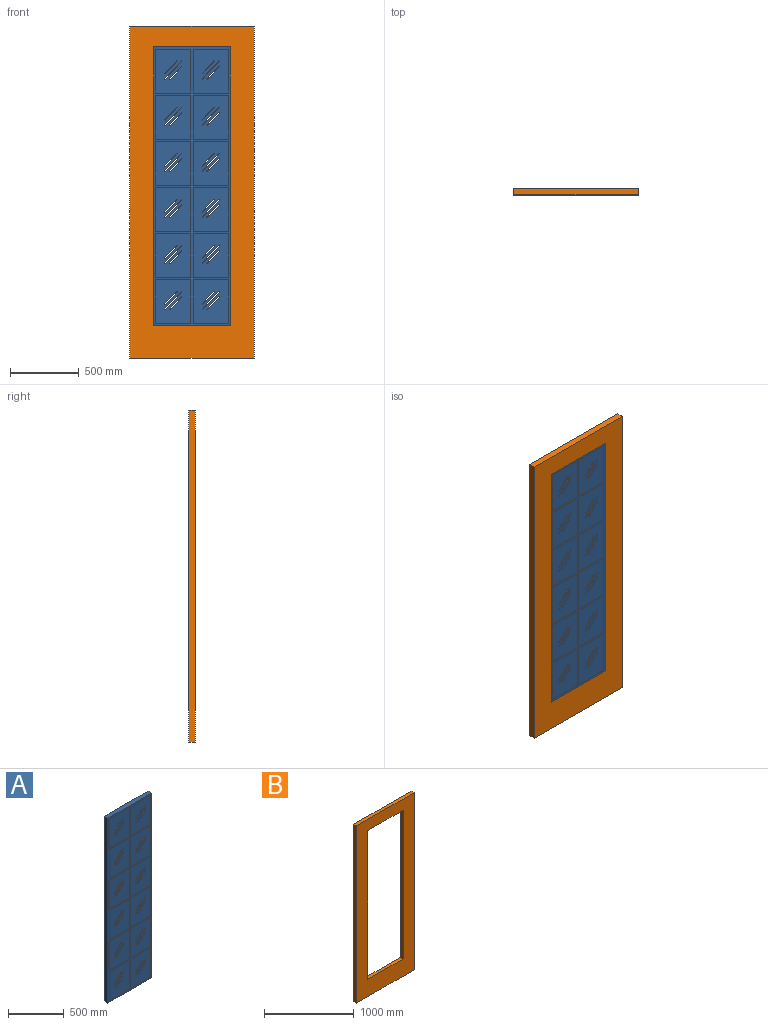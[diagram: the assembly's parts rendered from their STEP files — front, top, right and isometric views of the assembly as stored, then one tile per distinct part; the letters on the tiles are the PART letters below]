
ASSEMBLY  parts=2 mates=1
PART A: 270 faces, bbox 558.8x44.5x2032 mm
  f0: plane 320.15x0.64mm, normal (1,0,0), area 203.3mm2, adj f1,f3,f101,f269
  f1: plane 255.59x0.64mm, normal (0,0,-1), area 162.3mm2, adj f0,f2,f101,f269
  f2: plane 320.15x0.64mm, normal (-1,0,0), area 203.3mm2, adj f1,f3,f101,f269
  f3: plane 255.59x0.64mm, normal (0,0,1), area 162.3mm2, adj f0,f2,f101,f269
  f4: plane 255.59x0.64mm, normal (0,0,-1), area 162.3mm2, adj f5,f7,f101,f255
  f5: plane 320.15x0.64mm, normal (-1,0,0), area 203.3mm2, adj f4,f6,f101,f255
  f6: plane 255.59x0.64mm, normal (0,0,1), area 162.3mm2, adj f5,f7,f101,f255
  f7: plane 320.15x0.64mm, normal (1,0,0), area 203.3mm2, adj f4,f6,f101,f255
  f8: plane 320.15x0.64mm, normal (1,0,0), area 203.3mm2, adj f9,f11,f101,f241
  f9: plane 255.59x0.64mm, normal (0,0,-1), area 162.3mm2, adj f8,f10,f101,f241
  f10: plane 320.15x0.64mm, normal (-1,0,0), area 203.3mm2, adj f9,f11,f101,f241
  f11: plane 255.59x0.64mm, normal (0,0,1), area 162.3mm2, adj f8,f10,f101,f241
  f12: plane 320.15x0.64mm, normal (1,0,0), area 203.3mm2, adj f13,f15,f101,f227
  f13: plane 255.59x0.64mm, normal (0,0,-1), area 162.3mm2, adj f12,f14,f101,f227
  f14: plane 320.15x0.64mm, normal (-1,0,0), area 203.3mm2, adj f13,f15,f101,f227
  f15: plane 255.59x0.64mm, normal (0,0,1), area 162.3mm2, adj f12,f14,f101,f227
  f16: plane 255.59x0.64mm, normal (0,0,-1), area 162.3mm2, adj f17,f19,f101,f213
  f17: plane 320.15x0.64mm, normal (-1,0,0), area 203.3mm2, adj f16,f18,f101,f213
  f18: plane 255.59x0.64mm, normal (0,0,1), area 162.3mm2, adj f17,f19,f101,f213
  f19: plane 320.15x0.64mm, normal (1,0,0), area 203.3mm2, adj f16,f18,f101,f213
  f20: plane 320.15x0.64mm, normal (1,0,0), area 203.3mm2, adj f21,f23,f101,f199
  f21: plane 255.59x0.64mm, normal (0,0,-1), area 162.3mm2, adj f20,f22,f101,f199
  f22: plane 320.15x0.64mm, normal (-1,0,0), area 203.3mm2, adj f21,f23,f101,f199
  f23: plane 255.59x0.64mm, normal (0,0,1), area 162.3mm2, adj f20,f22,f101,f199
  f24: plane 320.15x0.64mm, normal (1,0,0), area 203.3mm2, adj f25,f27,f101,f185
  f25: plane 255.59x0.64mm, normal (0,0,-1), area 162.3mm2, adj f24,f26,f101,f185
  f26: plane 320.15x0.64mm, normal (-1,0,0), area 203.3mm2, adj f25,f27,f101,f185
  f27: plane 255.59x0.64mm, normal (0,0,1), area 162.3mm2, adj f24,f26,f101,f185
  f28: plane 255.59x0.64mm, normal (0,0,-1), area 162.3mm2, adj f29,f31,f101,f171
  f29: plane 320.15x0.64mm, normal (-1,0,0), area 203.3mm2, adj f28,f30,f101,f171
  f30: plane 255.59x0.64mm, normal (0,0,1), area 162.3mm2, adj f29,f31,f101,f171
  f31: plane 320.15x0.64mm, normal (1,0,0), area 203.3mm2, adj f28,f30,f101,f171
  f32: plane 255.59x0.64mm, normal (0,0,-1), area 162.3mm2, adj f33,f35,f101,f157
  f33: plane 320.15x0.64mm, normal (-1,0,0), area 203.3mm2, adj f32,f34,f101,f157
  f34: plane 255.59x0.64mm, normal (0,0,1), area 162.3mm2, adj f33,f35,f101,f157
  f35: plane 320.15x0.64mm, normal (1,0,0), area 203.3mm2, adj f32,f34,f101,f157
  f36: plane 320.15x0.64mm, normal (1,0,0), area 203.3mm2, adj f37,f39,f101,f143
  f37: plane 255.59x0.64mm, normal (0,0,-1), area 162.3mm2, adj f36,f38,f101,f143
  f38: plane 320.15x0.64mm, normal (-1,0,0), area 203.3mm2, adj f37,f39,f101,f143
  f39: plane 255.59x0.64mm, normal (0,0,1), area 162.3mm2, adj f36,f38,f101,f143
  f40: plane 320.15x0.64mm, normal (1,0,0), area 203.3mm2, adj f41,f43,f101,f129
  f41: plane 255.59x0.64mm, normal (0,0,-1), area 162.3mm2, adj f40,f42,f101,f129
  f42: plane 320.15x0.64mm, normal (-1,0,0), area 203.3mm2, adj f41,f43,f101,f129
  f43: plane 255.59x0.64mm, normal (0,0,1), area 162.3mm2, adj f40,f42,f101,f129
  f44: plane 255.59x0.64mm, normal (0,0,-1), area 162.3mm2, adj f45,f47,f101,f115
  f45: plane 320.15x0.64mm, normal (-1,0,0), area 203.3mm2, adj f44,f46,f101,f115
  f46: plane 255.59x0.64mm, normal (0,0,1), area 162.3mm2, adj f45,f47,f101,f115
  f47: plane 320.15x0.64mm, normal (1,0,0), area 203.3mm2, adj f44,f46,f101,f115
  f48: plane 320.15x0.64mm, normal (1,0,0), area 203.3mm2, adj f49,f99,f100,f268
  f49: plane 255.59x0.64mm, normal (0,0,-1), area 162.3mm2, adj f48,f50,f100,f268
  f50: plane 320.15x0.64mm, normal (-1,0,0), area 203.3mm2, adj f49,f99,f100,f268
  f51: plane 320.15x0.64mm, normal (1,0,0), area 203.3mm2, adj f52,f87,f100,f128
  f52: plane 255.59x0.64mm, normal (0,0,-1), area 162.3mm2, adj f51,f53,f100,f128
  f53: plane 320.15x0.64mm, normal (-1,0,0), area 203.3mm2, adj f52,f87,f100,f128
  f54: plane 320.15x0.64mm, normal (1,0,0), area 203.3mm2, adj f55,f88,f100,f142
  f55: plane 255.59x0.64mm, normal (0,0,-1), area 162.3mm2, adj f54,f56,f100,f142
  f56: plane 320.15x0.64mm, normal (-1,0,0), area 203.3mm2, adj f55,f88,f100,f142
  f57: plane 320.15x0.64mm, normal (1,0,0), area 203.3mm2, adj f58,f89,f100,f184
  f58: plane 255.59x0.64mm, normal (0,0,-1), area 162.3mm2, adj f57,f59,f100,f184
  f59: plane 320.15x0.64mm, normal (-1,0,0), area 203.3mm2, adj f58,f89,f100,f184
  f60: plane 320.15x0.64mm, normal (1,0,0), area 203.3mm2, adj f61,f90,f100,f198
  f61: plane 255.59x0.64mm, normal (0,0,-1), area 162.3mm2, adj f60,f62,f100,f198
  f62: plane 320.15x0.64mm, normal (-1,0,0), area 203.3mm2, adj f61,f90,f100,f198
  f63: plane 320.15x0.64mm, normal (1,0,0), area 203.3mm2, adj f64,f91,f100,f240
  f64: plane 255.59x0.64mm, normal (0,0,-1), area 162.3mm2, adj f63,f65,f100,f240
  f65: plane 320.15x0.64mm, normal (-1,0,0), area 203.3mm2, adj f64,f91,f100,f240
  f66: plane 320.15x0.64mm, normal (1,0,0), area 203.3mm2, adj f67,f92,f100,f226
  f67: plane 255.59x0.64mm, normal (0,0,-1), area 162.3mm2, adj f66,f68,f100,f226
  f68: plane 320.15x0.64mm, normal (-1,0,0), area 203.3mm2, adj f67,f92,f100,f226
  f69: plane 558.8x44.45mm, normal (0,0,1), area 24838.7mm2, adj f70,f93,f100,f101
  f70: plane 2032x44.45mm, normal (-1,0,0), area 90322.4mm2, adj f69,f71,f100,f101
  f71: plane 558.8x44.45mm, normal (0,0,-1), area 24838.7mm2, adj f70,f93,f100,f101
  f72: plane 255.59x0.64mm, normal (0,0,-1), area 162.3mm2, adj f73,f94,f100,f212
  f73: plane 320.15x0.64mm, normal (-1,0,0), area 203.3mm2, adj f72,f74,f100,f212
  f74: plane 255.59x0.64mm, normal (0,0,1), area 162.3mm2, adj f73,f94,f100,f212
  f75: plane 255.59x0.64mm, normal (0,0,-1), area 162.3mm2, adj f76,f95,f100,f170
  f76: plane 320.15x0.64mm, normal (-1,0,0), area 203.3mm2, adj f75,f77,f100,f170
  f77: plane 255.59x0.64mm, normal (0,0,1), area 162.3mm2, adj f76,f95,f100,f170
  f78: plane 255.59x0.64mm, normal (0,0,-1), area 162.3mm2, adj f79,f96,f100,f156
  f79: plane 320.15x0.64mm, normal (-1,0,0), area 203.3mm2, adj f78,f80,f100,f156
  f80: plane 255.59x0.64mm, normal (0,0,1), area 162.3mm2, adj f79,f96,f100,f156
  f81: plane 255.59x0.64mm, normal (0,0,-1), area 162.3mm2, adj f82,f97,f100,f114
  f82: plane 320.15x0.64mm, normal (-1,0,0), area 203.3mm2, adj f81,f83,f100,f114
  f83: plane 255.59x0.64mm, normal (0,0,1), area 162.3mm2, adj f82,f97,f100,f114
  f84: plane 255.59x0.64mm, normal (0,0,-1), area 162.3mm2, adj f85,f98,f100,f254
  f85: plane 320.15x0.64mm, normal (-1,0,0), area 203.3mm2, adj f84,f86,f100,f254
  f86: plane 255.59x0.64mm, normal (0,0,1), area 162.3mm2, adj f85,f98,f100,f254
  f87: plane 255.59x0.64mm, normal (0,0,1), area 162.3mm2, adj f51,f53,f100,f128
  f88: plane 255.59x0.64mm, normal (0,0,1), area 162.3mm2, adj f54,f56,f100,f142
  f89: plane 255.59x0.64mm, normal (0,0,1), area 162.3mm2, adj f57,f59,f100,f184
  f90: plane 255.59x0.64mm, normal (0,0,1), area 162.3mm2, adj f60,f62,f100,f198
  f91: plane 255.59x0.64mm, normal (0,0,1), area 162.3mm2, adj f63,f65,f100,f240
  f92: plane 255.59x0.64mm, normal (0,0,1), area 162.3mm2, adj f66,f68,f100,f226
  f93: plane 2032x44.45mm, normal (1,0,0), area 90322.4mm2, adj f69,f71,f100,f101
  f94: plane 320.15x0.64mm, normal (1,0,0), area 203.3mm2, adj f72,f74,f100,f212
  f95: plane 320.15x0.64mm, normal (1,0,0), area 203.3mm2, adj f75,f77,f100,f170
  f96: plane 320.15x0.64mm, normal (1,0,0), area 203.3mm2, adj f78,f80,f100,f156
  f97: plane 320.15x0.64mm, normal (1,0,0), area 203.3mm2, adj f81,f83,f100,f114
  f98: plane 320.15x0.64mm, normal (1,0,0), area 203.3mm2, adj f84,f86,f100,f254
  f99: plane 255.59x0.64mm, normal (0,0,1), area 162.3mm2, adj f48,f50,f100,f268
  f100: plane 2032x558.8mm, normal (0,-1,0), area 153578.3mm2, adj f48,f49,f50,f51,f52,f53,f54,f55
  f101: plane 2032x558.8mm, normal (0,1,0), area 153578.3mm2, adj f0,f1,f2,f3,f4,f5,f6,f7
  f102: cylinder r=3.17mm len=43.18mm, axis (0,1,0), area 430.7mm2, adj f103,f113,f114,f115
  f103: plane 88.11x82.76mm, normal (-0.73,0,0.68), area 5219.7mm2, adj f102,f104,f114,f115
  f104: cylinder r=3.17mm len=43.18mm, axis (0,1,0), area 430.7mm2, adj f103,f113,f114,f115
  f105: cylinder r=3.17mm len=43.18mm, axis (0,1,0), area 430.7mm2, adj f106,f111,f114,f115
  f106: plane 88.11x82.76mm, normal (-0.73,0,0.68), area 5219.7mm2, adj f105,f107,f114,f115
  f107: cylinder r=3.17mm len=43.18mm, axis (0,1,0), area 430.7mm2, adj f106,f111,f114,f115
  f108: plane 126.21x118.54mm, normal (0.73,0,-0.68), area 7476.7mm2, adj f109,f112,f114,f115
  f109: cylinder r=3.17mm len=43.18mm, axis (0,1,0), area 430.7mm2, adj f108,f110,f114,f115
  f110: plane 126.21x118.54mm, normal (-0.73,0,0.68), area 7476.7mm2, adj f109,f112,f114,f115
  f111: plane 88.11x82.76mm, normal (0.73,0,-0.68), area 5219.7mm2, adj f105,f107,f114,f115
  f112: cylinder r=3.17mm len=43.18mm, axis (0,1,0), area 430.7mm2, adj f108,f110,f114,f115
  f113: plane 88.11x82.76mm, normal (0.73,0,-0.68), area 5219.7mm2, adj f102,f104,f114,f115
  f114: plane 320.15x255.59mm, normal (0,-1,0), area 79095.5mm2, adj f81,f82,f83,f97,f102,f103,f104,f105
  f115: plane 320.15x255.59mm, normal (0,1,0), area 79095.5mm2, adj f44,f45,f46,f47,f102,f103,f104,f105
  f116: cylinder r=3.17mm len=43.18mm, axis (0,1,0), area 430.7mm2, adj f117,f127,f128,f129
  f117: plane 88.11x82.76mm, normal (-0.73,0,0.68), area 5219.7mm2, adj f116,f118,f128,f129
  f118: cylinder r=3.17mm len=43.18mm, axis (0,1,0), area 430.7mm2, adj f117,f127,f128,f129
  f119: cylinder r=3.17mm len=43.18mm, axis (0,1,0), area 430.7mm2, adj f120,f125,f128,f129
  f120: plane 88.11x82.76mm, normal (-0.73,0,0.68), area 5219.7mm2, adj f119,f121,f128,f129
  f121: cylinder r=3.17mm len=43.18mm, axis (0,1,0), area 430.7mm2, adj f120,f125,f128,f129
  f122: plane 126.21x118.54mm, normal (0.73,0,-0.68), area 7476.7mm2, adj f123,f126,f128,f129
  f123: cylinder r=3.17mm len=43.18mm, axis (0,1,0), area 430.7mm2, adj f122,f124,f128,f129
  f124: plane 126.21x118.54mm, normal (-0.73,0,0.68), area 7476.7mm2, adj f123,f126,f128,f129
  f125: plane 88.11x82.76mm, normal (0.73,0,-0.68), area 5219.7mm2, adj f119,f121,f128,f129
  f126: cylinder r=3.17mm len=43.18mm, axis (0,1,0), area 430.7mm2, adj f122,f124,f128,f129
  f127: plane 88.11x82.76mm, normal (0.73,0,-0.68), area 5219.7mm2, adj f116,f118,f128,f129
  f128: plane 320.15x255.59mm, normal (0,-1,0), area 79095.5mm2, adj f51,f52,f53,f87,f116,f117,f118,f119
  f129: plane 320.15x255.59mm, normal (0,1,0), area 79095.5mm2, adj f40,f41,f42,f43,f116,f117,f118,f119
  f130: cylinder r=3.17mm len=43.18mm, axis (0,1,0), area 430.7mm2, adj f131,f141,f142,f143
  f131: plane 88.11x82.76mm, normal (-0.73,0,0.68), area 5219.7mm2, adj f130,f132,f142,f143
  f132: cylinder r=3.17mm len=43.18mm, axis (0,1,0), area 430.7mm2, adj f131,f141,f142,f143
  f133: cylinder r=3.17mm len=43.18mm, axis (0,1,0), area 430.7mm2, adj f134,f139,f142,f143
  f134: plane 88.11x82.76mm, normal (-0.73,0,0.68), area 5219.7mm2, adj f133,f135,f142,f143
  f135: cylinder r=3.17mm len=43.18mm, axis (0,1,0), area 430.7mm2, adj f134,f139,f142,f143
  f136: plane 126.21x118.54mm, normal (0.73,0,-0.68), area 7476.7mm2, adj f137,f140,f142,f143
  f137: cylinder r=3.17mm len=43.18mm, axis (0,1,0), area 430.7mm2, adj f136,f138,f142,f143
  f138: plane 126.21x118.54mm, normal (-0.73,0,0.68), area 7476.7mm2, adj f137,f140,f142,f143
  f139: plane 88.11x82.76mm, normal (0.73,0,-0.68), area 5219.7mm2, adj f133,f135,f142,f143
  f140: cylinder r=3.17mm len=43.18mm, axis (0,1,0), area 430.7mm2, adj f136,f138,f142,f143
  f141: plane 88.11x82.76mm, normal (0.73,0,-0.68), area 5219.7mm2, adj f130,f132,f142,f143
  f142: plane 320.15x255.59mm, normal (0,-1,0), area 79095.5mm2, adj f54,f55,f56,f88,f130,f131,f132,f133
  f143: plane 320.15x255.59mm, normal (0,1,0), area 79095.5mm2, adj f36,f37,f38,f39,f130,f131,f132,f133
  f144: cylinder r=3.17mm len=43.18mm, axis (0,1,0), area 430.7mm2, adj f145,f155,f156,f157
  f145: plane 88.11x82.76mm, normal (-0.73,0,0.68), area 5219.7mm2, adj f144,f146,f156,f157
  f146: cylinder r=3.17mm len=43.18mm, axis (0,1,0), area 430.7mm2, adj f145,f155,f156,f157
  f147: cylinder r=3.17mm len=43.18mm, axis (0,1,0), area 430.7mm2, adj f148,f153,f156,f157
  f148: plane 88.11x82.76mm, normal (-0.73,0,0.68), area 5219.7mm2, adj f147,f149,f156,f157
  f149: cylinder r=3.17mm len=43.18mm, axis (0,1,0), area 430.7mm2, adj f148,f153,f156,f157
  f150: plane 126.21x118.54mm, normal (0.73,0,-0.68), area 7476.7mm2, adj f151,f154,f156,f157
  f151: cylinder r=3.17mm len=43.18mm, axis (0,1,0), area 430.7mm2, adj f150,f152,f156,f157
  f152: plane 126.21x118.54mm, normal (-0.73,0,0.68), area 7476.7mm2, adj f151,f154,f156,f157
  f153: plane 88.11x82.76mm, normal (0.73,0,-0.68), area 5219.7mm2, adj f147,f149,f156,f157
  f154: cylinder r=3.17mm len=43.18mm, axis (0,1,0), area 430.7mm2, adj f150,f152,f156,f157
  f155: plane 88.11x82.76mm, normal (0.73,0,-0.68), area 5219.7mm2, adj f144,f146,f156,f157
  f156: plane 320.15x255.59mm, normal (0,-1,0), area 79095.5mm2, adj f78,f79,f80,f96,f144,f145,f146,f147
  f157: plane 320.15x255.59mm, normal (0,1,0), area 79095.5mm2, adj f32,f33,f34,f35,f144,f145,f146,f147
  f158: cylinder r=3.17mm len=43.18mm, axis (0,1,0), area 430.7mm2, adj f159,f169,f170,f171
  f159: plane 88.11x82.76mm, normal (-0.73,0,0.68), area 5219.7mm2, adj f158,f160,f170,f171
  f160: cylinder r=3.17mm len=43.18mm, axis (0,1,0), area 430.7mm2, adj f159,f169,f170,f171
  f161: cylinder r=3.17mm len=43.18mm, axis (0,1,0), area 430.7mm2, adj f162,f167,f170,f171
  f162: plane 88.11x82.76mm, normal (-0.73,0,0.68), area 5219.7mm2, adj f161,f163,f170,f171
  f163: cylinder r=3.17mm len=43.18mm, axis (0,1,0), area 430.7mm2, adj f162,f167,f170,f171
  f164: plane 126.21x118.54mm, normal (0.73,0,-0.68), area 7476.7mm2, adj f165,f168,f170,f171
  f165: cylinder r=3.17mm len=43.18mm, axis (0,1,0), area 430.7mm2, adj f164,f166,f170,f171
  f166: plane 126.21x118.54mm, normal (-0.73,0,0.68), area 7476.7mm2, adj f165,f168,f170,f171
  f167: plane 88.11x82.76mm, normal (0.73,0,-0.68), area 5219.7mm2, adj f161,f163,f170,f171
  f168: cylinder r=3.17mm len=43.18mm, axis (0,1,0), area 430.7mm2, adj f164,f166,f170,f171
  f169: plane 88.11x82.76mm, normal (0.73,0,-0.68), area 5219.7mm2, adj f158,f160,f170,f171
  f170: plane 320.15x255.59mm, normal (0,-1,0), area 79095.5mm2, adj f75,f76,f77,f95,f158,f159,f160,f161
  f171: plane 320.15x255.59mm, normal (0,1,0), area 79095.5mm2, adj f28,f29,f30,f31,f158,f159,f160,f161
  f172: cylinder r=3.17mm len=43.18mm, axis (0,1,0), area 430.7mm2, adj f173,f183,f184,f185
  f173: plane 88.11x82.76mm, normal (-0.73,0,0.68), area 5219.7mm2, adj f172,f174,f184,f185
  f174: cylinder r=3.17mm len=43.18mm, axis (0,1,0), area 430.7mm2, adj f173,f183,f184,f185
  f175: cylinder r=3.17mm len=43.18mm, axis (0,1,0), area 430.7mm2, adj f176,f181,f184,f185
  f176: plane 88.11x82.76mm, normal (-0.73,0,0.68), area 5219.7mm2, adj f175,f177,f184,f185
  f177: cylinder r=3.17mm len=43.18mm, axis (0,1,0), area 430.7mm2, adj f176,f181,f184,f185
  f178: plane 126.21x118.54mm, normal (0.73,0,-0.68), area 7476.7mm2, adj f179,f182,f184,f185
  f179: cylinder r=3.17mm len=43.18mm, axis (0,1,0), area 430.7mm2, adj f178,f180,f184,f185
  f180: plane 126.21x118.54mm, normal (-0.73,0,0.68), area 7476.7mm2, adj f179,f182,f184,f185
  f181: plane 88.11x82.76mm, normal (0.73,0,-0.68), area 5219.7mm2, adj f175,f177,f184,f185
  f182: cylinder r=3.17mm len=43.18mm, axis (0,1,0), area 430.7mm2, adj f178,f180,f184,f185
  f183: plane 88.11x82.76mm, normal (0.73,0,-0.68), area 5219.7mm2, adj f172,f174,f184,f185
  f184: plane 320.15x255.59mm, normal (0,-1,0), area 79095.5mm2, adj f57,f58,f59,f89,f172,f173,f174,f175
  f185: plane 320.15x255.59mm, normal (0,1,0), area 79095.5mm2, adj f24,f25,f26,f27,f172,f173,f174,f175
  f186: cylinder r=3.17mm len=43.18mm, axis (0,1,0), area 430.7mm2, adj f187,f197,f198,f199
  f187: plane 88.11x82.76mm, normal (-0.73,0,0.68), area 5219.7mm2, adj f186,f188,f198,f199
  f188: cylinder r=3.17mm len=43.18mm, axis (0,1,0), area 430.7mm2, adj f187,f197,f198,f199
  f189: cylinder r=3.17mm len=43.18mm, axis (0,1,0), area 430.7mm2, adj f190,f195,f198,f199
  f190: plane 88.11x82.76mm, normal (-0.73,0,0.68), area 5219.7mm2, adj f189,f191,f198,f199
  f191: cylinder r=3.17mm len=43.18mm, axis (0,1,0), area 430.7mm2, adj f190,f195,f198,f199
  f192: plane 126.21x118.54mm, normal (0.73,0,-0.68), area 7476.7mm2, adj f193,f196,f198,f199
  f193: cylinder r=3.17mm len=43.18mm, axis (0,1,0), area 430.7mm2, adj f192,f194,f198,f199
  f194: plane 126.21x118.54mm, normal (-0.73,0,0.68), area 7476.7mm2, adj f193,f196,f198,f199
  f195: plane 88.11x82.76mm, normal (0.73,0,-0.68), area 5219.7mm2, adj f189,f191,f198,f199
  f196: cylinder r=3.17mm len=43.18mm, axis (0,1,0), area 430.7mm2, adj f192,f194,f198,f199
  f197: plane 88.11x82.76mm, normal (0.73,0,-0.68), area 5219.7mm2, adj f186,f188,f198,f199
  f198: plane 320.15x255.59mm, normal (0,-1,0), area 79095.5mm2, adj f60,f61,f62,f90,f186,f187,f188,f189
  f199: plane 320.15x255.59mm, normal (0,1,0), area 79095.5mm2, adj f20,f21,f22,f23,f186,f187,f188,f189
  f200: cylinder r=3.17mm len=43.18mm, axis (0,1,0), area 430.7mm2, adj f201,f211,f212,f213
  f201: plane 88.11x82.76mm, normal (-0.73,0,0.68), area 5219.7mm2, adj f200,f202,f212,f213
  f202: cylinder r=3.17mm len=43.18mm, axis (0,1,0), area 430.7mm2, adj f201,f211,f212,f213
  f203: cylinder r=3.17mm len=43.18mm, axis (0,1,0), area 430.7mm2, adj f204,f209,f212,f213
  f204: plane 88.11x82.76mm, normal (-0.73,0,0.68), area 5219.7mm2, adj f203,f205,f212,f213
  f205: cylinder r=3.17mm len=43.18mm, axis (0,1,0), area 430.7mm2, adj f204,f209,f212,f213
  f206: plane 126.21x118.54mm, normal (0.73,0,-0.68), area 7476.7mm2, adj f207,f210,f212,f213
  f207: cylinder r=3.17mm len=43.18mm, axis (0,1,0), area 430.7mm2, adj f206,f208,f212,f213
  f208: plane 126.21x118.54mm, normal (-0.73,0,0.68), area 7476.7mm2, adj f207,f210,f212,f213
  f209: plane 88.11x82.76mm, normal (0.73,0,-0.68), area 5219.7mm2, adj f203,f205,f212,f213
  f210: cylinder r=3.17mm len=43.18mm, axis (0,1,0), area 430.7mm2, adj f206,f208,f212,f213
  f211: plane 88.11x82.76mm, normal (0.73,0,-0.68), area 5219.7mm2, adj f200,f202,f212,f213
  f212: plane 320.15x255.59mm, normal (0,-1,0), area 79095.5mm2, adj f72,f73,f74,f94,f200,f201,f202,f203
  f213: plane 320.15x255.59mm, normal (0,1,0), area 79095.5mm2, adj f16,f17,f18,f19,f200,f201,f202,f203
  f214: plane 88.11x82.76mm, normal (-0.73,0,0.68), area 5219.7mm2, adj f215,f225,f226,f227
  f215: cylinder r=3.17mm len=43.18mm, axis (0,1,0), area 430.7mm2, adj f214,f216,f226,f227
  f216: plane 88.11x82.76mm, normal (0.73,0,-0.68), area 5219.7mm2, adj f215,f225,f226,f227
  f217: plane 88.11x82.76mm, normal (-0.73,0,0.68), area 5219.7mm2, adj f218,f223,f226,f227
  f218: cylinder r=3.17mm len=43.18mm, axis (0,1,0), area 430.7mm2, adj f217,f219,f226,f227
  f219: plane 88.11x82.76mm, normal (0.73,0,-0.68), area 5219.7mm2, adj f218,f223,f226,f227
  f220: plane 126.21x118.54mm, normal (-0.73,0,0.68), area 7476.7mm2, adj f221,f224,f226,f227
  f221: cylinder r=3.17mm len=43.18mm, axis (0,1,0), area 430.7mm2, adj f220,f222,f226,f227
  f222: plane 126.21x118.54mm, normal (0.73,0,-0.68), area 7476.7mm2, adj f221,f224,f226,f227
  f223: cylinder r=3.17mm len=43.18mm, axis (0,1,0), area 430.7mm2, adj f217,f219,f226,f227
  f224: cylinder r=3.17mm len=43.18mm, axis (0,1,0), area 430.7mm2, adj f220,f222,f226,f227
  f225: cylinder r=3.17mm len=43.18mm, axis (0,1,0), area 430.7mm2, adj f214,f216,f226,f227
  f226: plane 320.15x255.59mm, normal (0,-1,0), area 79095.5mm2, adj f66,f67,f68,f92,f214,f215,f216,f217
  f227: plane 320.15x255.59mm, normal (0,1,0), area 79095.5mm2, adj f12,f13,f14,f15,f214,f215,f216,f217
  f228: cylinder r=3.17mm len=43.18mm, axis (0,1,0), area 430.7mm2, adj f229,f239,f240,f241
  f229: plane 88.11x82.76mm, normal (-0.73,0,0.68), area 5219.7mm2, adj f228,f230,f240,f241
  f230: cylinder r=3.17mm len=43.18mm, axis (0,1,0), area 430.7mm2, adj f229,f239,f240,f241
  f231: cylinder r=3.17mm len=43.18mm, axis (0,1,0), area 430.7mm2, adj f232,f237,f240,f241
  f232: plane 88.11x82.76mm, normal (-0.73,0,0.68), area 5219.7mm2, adj f231,f233,f240,f241
  f233: cylinder r=3.17mm len=43.18mm, axis (0,1,0), area 430.7mm2, adj f232,f237,f240,f241
  f234: plane 126.21x118.54mm, normal (0.73,0,-0.68), area 7476.7mm2, adj f235,f238,f240,f241
  f235: cylinder r=3.17mm len=43.18mm, axis (0,1,0), area 430.7mm2, adj f234,f236,f240,f241
  f236: plane 126.21x118.54mm, normal (-0.73,0,0.68), area 7476.7mm2, adj f235,f238,f240,f241
  f237: plane 88.11x82.76mm, normal (0.73,0,-0.68), area 5219.7mm2, adj f231,f233,f240,f241
  f238: cylinder r=3.17mm len=43.18mm, axis (0,1,0), area 430.7mm2, adj f234,f236,f240,f241
  f239: plane 88.11x82.76mm, normal (0.73,0,-0.68), area 5219.7mm2, adj f228,f230,f240,f241
  f240: plane 320.15x255.59mm, normal (0,-1,0), area 79095.5mm2, adj f63,f64,f65,f91,f228,f229,f230,f231
  f241: plane 320.15x255.59mm, normal (0,1,0), area 79095.5mm2, adj f8,f9,f10,f11,f228,f229,f230,f231
  f242: cylinder r=3.17mm len=43.18mm, axis (0,1,0), area 430.7mm2, adj f243,f253,f254,f255
  f243: plane 88.11x82.76mm, normal (-0.73,0,0.68), area 5219.7mm2, adj f242,f244,f254,f255
  f244: cylinder r=3.17mm len=43.18mm, axis (0,1,0), area 430.7mm2, adj f243,f253,f254,f255
  f245: cylinder r=3.17mm len=43.18mm, axis (0,1,0), area 430.7mm2, adj f246,f251,f254,f255
  f246: plane 88.11x82.76mm, normal (-0.73,0,0.68), area 5219.7mm2, adj f245,f247,f254,f255
  f247: cylinder r=3.17mm len=43.18mm, axis (0,1,0), area 430.7mm2, adj f246,f251,f254,f255
  f248: plane 126.21x118.54mm, normal (0.73,0,-0.68), area 7476.7mm2, adj f249,f252,f254,f255
  f249: cylinder r=3.17mm len=43.18mm, axis (0,1,0), area 430.7mm2, adj f248,f250,f254,f255
  f250: plane 126.21x118.54mm, normal (-0.73,0,0.68), area 7476.7mm2, adj f249,f252,f254,f255
  f251: plane 88.11x82.76mm, normal (0.73,0,-0.68), area 5219.7mm2, adj f245,f247,f254,f255
  f252: cylinder r=3.17mm len=43.18mm, axis (0,1,0), area 430.7mm2, adj f248,f250,f254,f255
  f253: plane 88.11x82.76mm, normal (0.73,0,-0.68), area 5219.7mm2, adj f242,f244,f254,f255
  f254: plane 320.15x255.59mm, normal (0,-1,0), area 79095.5mm2, adj f84,f85,f86,f98,f242,f243,f244,f245
  f255: plane 320.15x255.59mm, normal (0,1,0), area 79095.5mm2, adj f4,f5,f6,f7,f242,f243,f244,f245
  f256: cylinder r=3.17mm len=43.18mm, axis (0,1,0), area 430.7mm2, adj f257,f267,f268,f269
  f257: plane 88.11x82.76mm, normal (-0.73,0,0.68), area 5219.7mm2, adj f256,f258,f268,f269
  f258: cylinder r=3.17mm len=43.18mm, axis (0,1,0), area 430.7mm2, adj f257,f267,f268,f269
  f259: cylinder r=3.17mm len=43.18mm, axis (0,1,0), area 430.7mm2, adj f260,f265,f268,f269
  f260: plane 88.11x82.76mm, normal (-0.73,0,0.68), area 5219.7mm2, adj f259,f261,f268,f269
  f261: cylinder r=3.17mm len=43.18mm, axis (0,1,0), area 430.7mm2, adj f260,f265,f268,f269
  f262: plane 126.21x118.54mm, normal (0.73,0,-0.68), area 7476.7mm2, adj f263,f266,f268,f269
  f263: cylinder r=3.17mm len=43.18mm, axis (0,1,0), area 430.7mm2, adj f262,f264,f268,f269
  f264: plane 126.21x118.54mm, normal (-0.73,0,0.68), area 7476.7mm2, adj f263,f266,f268,f269
  f265: plane 88.11x82.76mm, normal (0.73,0,-0.68), area 5219.7mm2, adj f259,f261,f268,f269
  f266: cylinder r=3.17mm len=43.18mm, axis (0,1,0), area 430.7mm2, adj f262,f264,f268,f269
  f267: plane 88.11x82.76mm, normal (0.73,0,-0.68), area 5219.7mm2, adj f256,f258,f268,f269
  f268: plane 320.15x255.59mm, normal (0,-1,0), area 79095.5mm2, adj f48,f49,f50,f99,f256,f257,f258,f259
  f269: plane 320.15x255.59mm, normal (0,1,0), area 79095.5mm2, adj f0,f1,f2,f3,f256,f257,f258,f259
PART B: 10 faces, bbox 908.1x44.5x2419.4 mm
  f0: plane 908.05x44.45mm, normal (0,0,1), area 40362.8mm2, adj f1,f7,f8,f9
  f1: plane 2419.35x44.45mm, normal (-1,0,0), area 107540.1mm2, adj f0,f2,f8,f9
  f2: plane 908.05x44.45mm, normal (0,0,-1), area 40362.8mm2, adj f1,f7,f8,f9
  f3: plane 558.8x44.45mm, normal (0,0,1), area 24838.7mm2, adj f4,f6,f8,f9
  f4: plane 2032x44.45mm, normal (1,0,0), area 90322.4mm2, adj f3,f5,f8,f9
  f5: plane 558.8x44.45mm, normal (0,0,-1), area 24838.7mm2, adj f4,f6,f8,f9
  f6: plane 2032x44.45mm, normal (-1,0,0), area 90322.4mm2, adj f3,f5,f8,f9
  f7: plane 2419.35x44.45mm, normal (1,0,0), area 107540.1mm2, adj f0,f2,f8,f9
  f8: plane 2419.35x908.05mm, normal (0,-1,0), area 1061409.2mm2, adj f0,f1,f2,f3,f4,f5,f6,f7
  f9: plane 2419.35x908.05mm, normal (0,1,0), area 1061409.2mm2, adj f0,f1,f2,f3,f4,f5,f6,f7
PLACE A t=(-646.59,426.03,-17.68)mm
PLACE B t=(-821.21,426.03,-252.63)mm
MATE fastened A.f69 <-> B.f5  axis (0,0,1) through (-367.19,426.03,2014.32)mm
